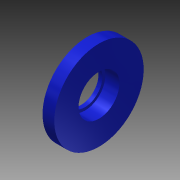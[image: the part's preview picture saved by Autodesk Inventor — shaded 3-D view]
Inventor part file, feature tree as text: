
AUTODESK INVENTOR PART (.ipt)
format: ipt  version: 2014 (Build 180170000, 170)  size: 116,736 bytes
history: native  units: in
note: dims shown in document units (in); Inventor stores cm internally (conversion verified against a paired STEP export)
features: reference x7, sketch x1, other x1, revolve x1, fillet x1
ambient origin geometry x8: Origin, YZ Plane, XZ Plane, XY Plane, X Axis, Y Axis, Z Axis, Center Point
bodies: Solid1 (feature_tree)
feature tree (11):
  sketch  "Sketch1"  dims[d0=0.025in d1=0.025in d2=0.01in d3=0.01in d4=0.01in d5=0.1in d6=0.1in d7=0.075in d8=90.0deg d9=0.125in]
  other  "Work Axis1"
  revolve  "Revolution1"  [1 undecoded]
  fillet  "Fillet1"  Radius=0.01in
  reference  "Reference1"
  reference  "Reference2"
  reference  "Reference3"
  reference  "Reference4"
  reference  "Reference5"
  reference  "Reference6"
  reference  "Reference7"
note: 1 required parameter value undecoded (feature->parameter linkage not recoverable at this tier; creation-order binding heuristic only, values carry confidence <= 0.55)
